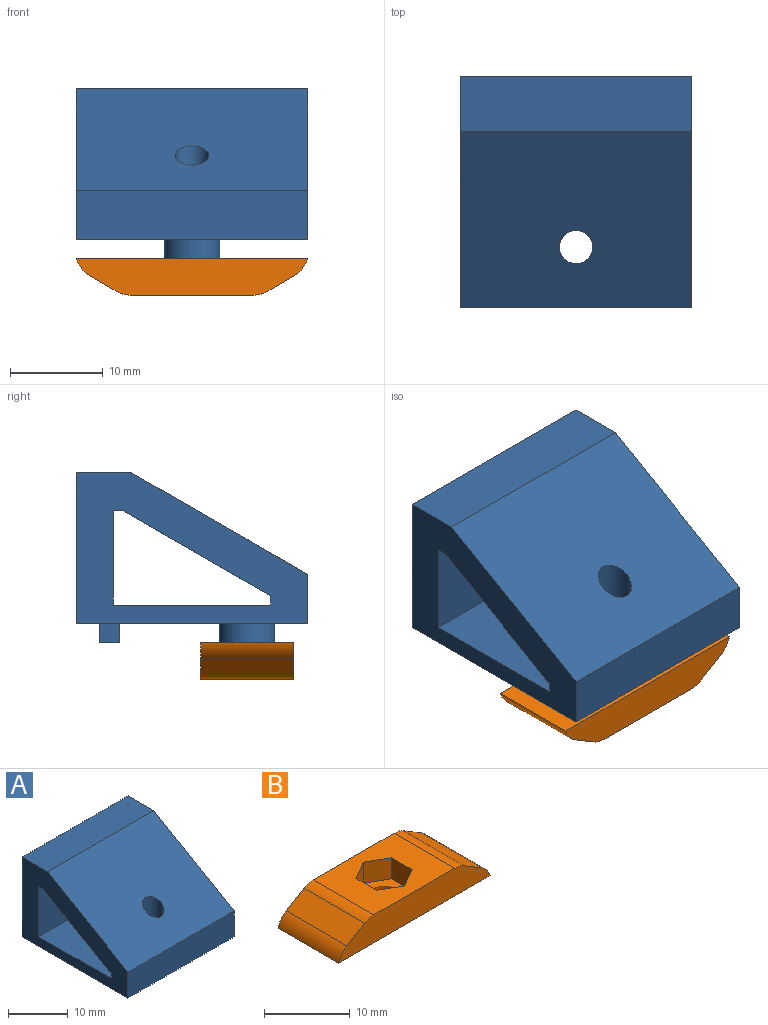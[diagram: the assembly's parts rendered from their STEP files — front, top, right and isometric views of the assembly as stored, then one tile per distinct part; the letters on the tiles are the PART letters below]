
ASSEMBLY  parts=2 mates=1
PART A: 28 faces, bbox 25x25x18.3 mm
  f0: plane 25x16.28mm, normal (0,1,0), area 348.4mm2, adj f1,f4,f5,f10,f22,f23,f24,f25
  f1: plane 25x25mm, normal (0,0,-1), area 585.7mm2, adj f0,f3,f4,f5,f12,f13,f14,f15
  f2: plane 25x17mm, normal (0,0,1), area 414.8mm2, adj f4,f5,f8,f11,f20
  f3: plane 25x5.31mm, normal (0,-1,0), area 132.7mm2, adj f1,f4,f5,f9
  f4: plane 25x16.28mm, normal (1,0,0), area 202.6mm2, adj f0,f1,f2,f3,f6,f7,f8,f9
  f5: plane 25x16.28mm, normal (-1,0,0), area 202.6mm2, adj f0,f1,f2,f3,f6,f7,f8,f9
  f6: plane 25x1mm, normal (0,0,-1), area 25mm2, adj f4,f5,f7,f11,f21
  f7: plane 25x16mm, normal (0,0.5,-0.87), area 450.1mm2, adj f4,f5,f6,f8,f19
  f8: plane 25x1mm, normal (0,1,0), area 25mm2, adj f2,f4,f5,f7
  f9: plane 25x19mm, normal (0,-0.5,0.87), area 536.7mm2, adj f3,f4,f5,f10,f19
  f10: plane 25x6mm, normal (0,0,1), area 150mm2, adj f0,f4,f5,f9
  f11: plane 25x10.24mm, normal (0,-1,0), area 197.4mm2, adj f2,f4,f5,f6,f23,f24,f25,f26
  f12: plane 2.2x2mm, normal (1,0,0), area 4.4mm2, adj f1,f13,f15,f16
  f13: plane 5x2mm, normal (0,-1,0), area 10mm2, adj f1,f12,f14,f16
  f14: plane 2.2x2mm, normal (-1,0,0), area 4.4mm2, adj f1,f13,f15,f16
  f15: plane 5x2mm, normal (0,1,0), area 10mm2, adj f1,f12,f14,f16
  f16: plane 5x2.2mm, normal (0,0,-1), area 11mm2, adj f12,f13,f14,f15
  f17: cylinder r=3mm len=6mm, axis (0,0,1), area 37.7mm2, adj f1,f18
  f18: plane 6x6mm, normal (0,0,-1), area 18.1mm2, adj f17,f20
  f19: cylinder r=1.8mm len=6.71mm, axis (0,0,-1), area 52.2mm2, adj f7,f9
  f20: cylinder r=1.8mm len=4mm, axis (0,0,-1), area 45.2mm2, adj f2,f18
  f21: plane 4.77x0.02mm, normal (0,1,0), area 0.1mm2, adj f6,f22,f23,f25
  f22: plane 4.75x4mm, normal (0,0,-1), area 19mm2, adj f0,f21,f23,f25
  f23: plane 4.11x4mm, normal (-0.87,0,-0.5), area 19mm2, adj f0,f11,f21,f22,f24
  f24: plane 4.11x4mm, normal (-0.87,0,0.5), area 19mm2, adj f0,f11,f23,f26
  f25: plane 4.11x4mm, normal (0.87,0,-0.5), area 19mm2, adj f0,f11,f21,f22,f27
  f26: plane 4.75x4mm, normal (0,0,1), area 19mm2, adj f0,f11,f24,f27
  f27: plane 4.11x4mm, normal (0.87,0,0.5), area 19mm2, adj f0,f11,f25,f26
PART B: 18 faces, bbox 25x10x4 mm
  f0: plane 13.34x10mm, normal (0,0,1), area 103.3mm2, adj f1,f2,f4,f5,f6,f7,f8,f9
  f1: plane 25x4mm, normal (0,-1,0), area 84.2mm2, adj f0,f3,f12,f13,f14,f15,f16,f17
  f2: plane 25x4mm, normal (0,1,0), area 84.2mm2, adj f0,f3,f12,f13,f14,f15,f16,f17
  f3: plane 25x10mm, normal (0,0,-1), area 239.8mm2, adj f1,f2,f11,f14,f17
  f4: plane 3x2.94mm, normal (-0.5,-0.87,0), area 10.2mm2, adj f0,f5,f9,f10
  f5: plane 3x2.94mm, normal (0.5,-0.87,0), area 10.2mm2, adj f0,f4,f6,f10
  f6: plane 3.4x3mm, normal (1,0,0), area 10.2mm2, adj f0,f5,f7,f10
  f7: plane 3x2.94mm, normal (0.5,0.87,0), area 10.2mm2, adj f0,f6,f8,f10
  f8: plane 3x2.94mm, normal (-0.5,0.87,0), area 10.2mm2, adj f0,f7,f9,f10
  f9: plane 3.4x3mm, normal (-1,0,0), area 10.2mm2, adj f0,f4,f8,f10
  f10: plane 6.8x5.89mm, normal (0,0,1), area 19.9mm2, adj f4,f5,f6,f7,f8,f9,f11
  f11: cylinder r=1.8mm len=3.6mm, axis (0,0,1), area 11.3mm2, adj f3,f10
  f12: plane 10x2.93mm, normal (0.51,0,0.86), area 34.1mm2, adj f1,f2,f14,f15
  f13: plane 10x2.93mm, normal (-0.51,0,0.86), area 34.1mm2, adj f1,f2,f16,f17
  f14: cylinder r=3mm len=10mm, axis (0,-1,0), area 23.3mm2, adj f1,f2,f3,f12
  f15: cylinder r=3mm len=10mm, axis (0,-1,0), area 16.2mm2, adj f0,f1,f2,f12
  f16: cylinder r=3mm len=10mm, axis (0,1,0), area 16.2mm2, adj f0,f1,f2,f13
  f17: cylinder r=3mm len=10mm, axis (0,-1,0), area 23.3mm2, adj f1,f2,f3,f13
PLACE A t=(-11.11,4.67,5.46)mm
PLACE B rot(axis=(1,0,0),180deg) t=(-11.11,-1.28,3.46)mm
MATE fastened B.f11 <-> A.f17  axis (0,0,-1) through (-11.11,-1.28,3.46)mm
